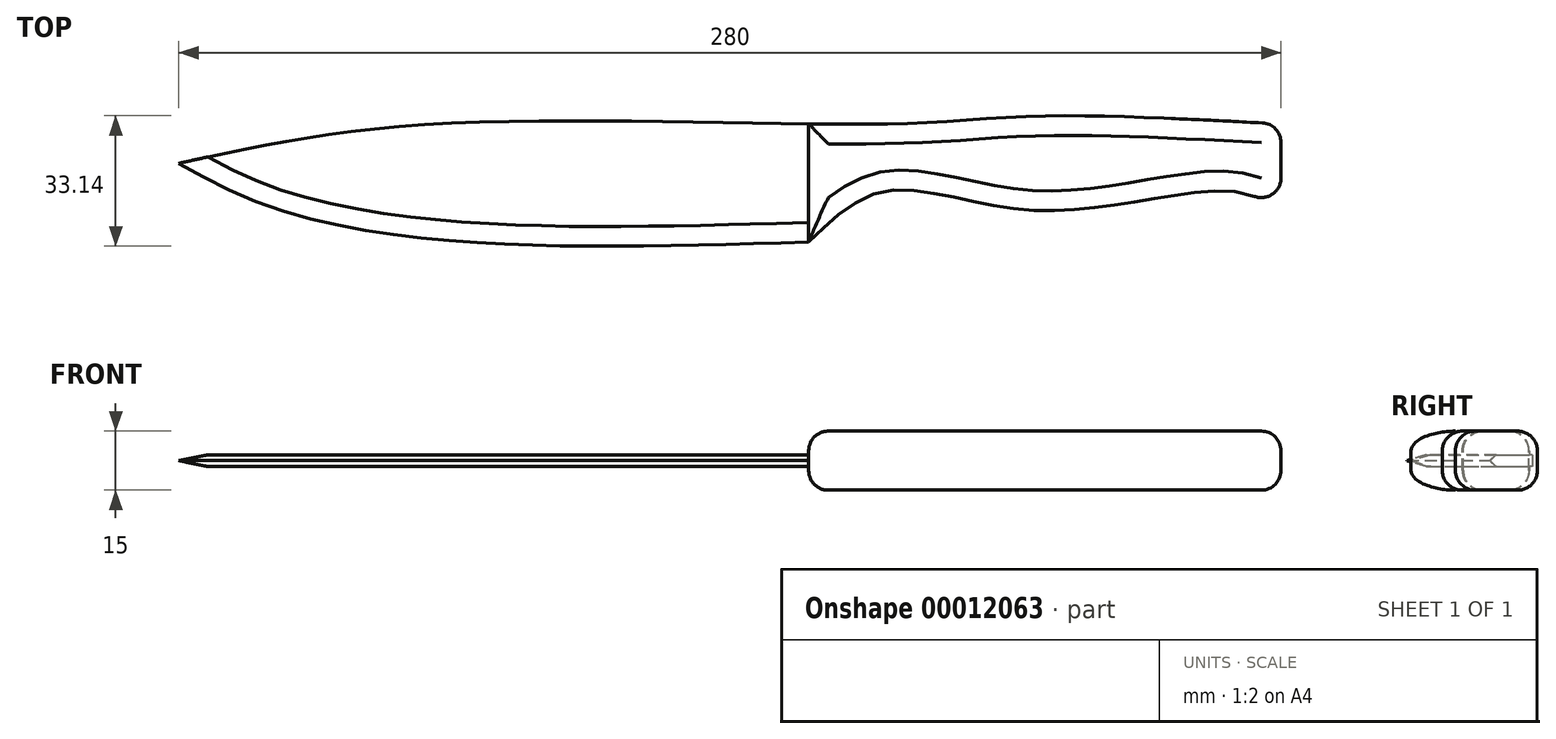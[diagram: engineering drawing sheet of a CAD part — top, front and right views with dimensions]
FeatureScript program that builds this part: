
annotation { "Feature Type Name" : "Feature", "Feature Type Description" : "" }
export const myFeature = defineFeature(function(context is Context, id is Id, definition is map)
    precondition{}
    {
        {
            var Q0;
            Q0=qCreatedBy(makeId("Top.planeOp"),FACE);
            var sketch = newSketch(context, id + "F0", { "sketchPlane" : qUnion([Q0])});
            skLineSegment(sketch, "E0", {"start": v(-162.75, 0) * mm, "end": v(117.25, 0) * mm, "construction": true});
            skLineSegment(sketch, "E1", {"start": v(-2.75, -20) * mm, "end": v(-2.75, 10) * mm});
            skLineSegment(sketch, "E2", {"start": v(17.25, -7) * mm, "end": v(17.25, 10) * mm, "construction": true});
            skLineSegment(sketch, "E3", {"start": v(117.25, 10) * mm, "end": v(117.25, -12) * mm});
            skLineSegment(sketch, "E4", {"start": v(103.55, 0) * mm, "end": v(103.55, -7) * mm, "construction": true});
            skLineSegment(sketch, "E5", {"start": v(55.6, 0) * mm, "end": v(55.6, 12) * mm, "construction": true});
            skLineSegment(sketch, "E6", {"start": v(55.6, 0) * mm, "end": v(55.6, -12) * mm, "construction": true});
            skFitSpline(sketch, "E7", {"points": [v(-162.75, 0) * mm, v(-96.94, 10) * mm, v(17.25, 10) * mm, v(55.6, 12) * mm, v(117.25, 10) * mm], "startDerivative": vector(232.14, 51.12) * mm, "endDerivative": vector(284.39, -15.23) * mm});
            skFitSpline(sketch, "E8", {"points": [v(117.25, -12) * mm, v(103.55, -7) * mm, v(55.6, -12) * mm, v(17.25, -7) * mm, v(-2.75, -20) * mm], "startDerivative": vector(-64.1, 40.3) * mm, "endDerivative": vector(-81.22, -79.08) * mm});
            skFitSpline(sketch, "E9", {"points": [v(-2.75, -20) * mm, v(-89.64, -20) * mm, v(-139.33, -11.16) * mm, v(-162.75, 0) * mm], "startDerivative": vector(-211.22, -6.31) * mm, "endDerivative": vector(-89.85, 50.4) * mm});
            skSolve(sketch);
        }
        {
            var Q0;
            {var subQ0=sQuery(id+"F0.wireOp",EDGE,"E9");Q0=makeQuery(id+"F0.imprint","IMPRINT",FACE,{"disambiguationData":[TD([[makeQuery(id+"F0.imprint","IMPRINT",EDGE,{"derivedFrom":subQ0}),-1.0]])]});}
            extrude(context, id + "F1", {"entities" : qUnion([Q0]), "endBound" : BoundingType.SYMMETRIC, "depth" : 3 * mm});
        }
        {
            var Q0;
            {var subQ4=sQuery(id+"F0.wireOp",EDGE,"E3");Q0=makeQuery(id+"F0.imprint","IMPRINT",FACE,{"disambiguationData":[TD([[makeQuery(id+"F0.imprint","IMPRINT",EDGE,{"derivedFrom":subQ4}),-1.0]])]});}
            extrude(context, id + "F2", {"entities" : qUnion([Q0]), "operationType" : NewBodyOperationType.ADD, "endBound" : BoundingType.SYMMETRIC, "depth" : 15 * mm});
        }
        {
            var Q0;
            Q0=makeQuery(id+"F2.opExtrude","CAP_EDGE",EDGE,{"disambiguationData":[OSD([sQuery(id+"F0.wireOp",EDGE,"E8")])],"isStart":false});
            var Q1;
            Q1=makeQuery(id+"F2.opExtrude","CAP_EDGE",EDGE,{"disambiguationData":[OSD([sQuery(id+"F0.wireOp",EDGE,"E1")])],"isStart":false});
            var Q2;
            Q2=makeQuery(id+"F2.opExtrude","CAP_EDGE",EDGE,{"disambiguationData":[OSD([sQuery(id+"F0.wireOp",EDGE,"E7")])],"isStart":false});
            var Q3;
            Q3=makeQuery(id+"F2.opExtrude","CAP_EDGE",EDGE,{"disambiguationData":[OSD([sQuery(id+"F0.wireOp",EDGE,"E3")])],"isStart":false});
            var Q4;
            Q4=makeQuery(id+"F2.opExtrude","CAP_EDGE",EDGE,{"disambiguationData":[OSD([sQuery(id+"F0.wireOp",EDGE,"E1")])],"isStart":true});
            var Q5;
            Q5=makeQuery(id+"F2.opExtrude","CAP_EDGE",EDGE,{"disambiguationData":[OSD([sQuery(id+"F0.wireOp",EDGE,"E7")])],"isStart":true});
            var Q6;
            Q6=makeQuery(id+"F2.opExtrude","CAP_EDGE",EDGE,{"disambiguationData":[OSD([sQuery(id+"F0.wireOp",EDGE,"E8")])],"isStart":true});
            var Q7;
            Q7=makeQuery(id+"F2.opExtrude","CAP_EDGE",EDGE,{"disambiguationData":[OSD([sQuery(id+"F0.wireOp",EDGE,"E3")])],"isStart":true});
            var Q8;
            Q8=makeQuery(id+"F2.opExtrude","SWEPT_EDGE",EDGE,{"disambiguationData":[OSD([sQuery(id+"F0.wireOp",EDGE,"E3"),sQuery(id+"F0.wireOp",EDGE,"E8")])]});
            var Q9;
            Q9=makeQuery(id+"F2.opExtrude","SWEPT_EDGE",EDGE,{"disambiguationData":[OSD([sQuery(id+"F0.wireOp",EDGE,"E3"),sQuery(id+"F0.wireOp",EDGE,"E7")])]});
            fillet(context, id + "F3", {"entities" : qUnion([Q0, Q1, Q2, Q3, Q4, Q5, Q6, Q7, Q8, Q9]), "radius" : 5 * mm, "tangentPropagation" : true, "allowEdgeOverflow" : false});
        }
        {
            var Q0;
            Q0=makeQuery(id+"F1.opExtrude","CAP_EDGE",EDGE,{"disambiguationData":[OSD([sQuery(id+"F0.wireOp",EDGE,"E9")])],"isStart":true});
            var Q1;
            Q1=makeQuery(id+"F1.opExtrude","CAP_EDGE",EDGE,{"disambiguationData":[OSD([sQuery(id+"F0.wireOp",EDGE,"E9")])],"isStart":false});
            chamfer(context, id + "F4", {"entities" : qUnion([Q0, Q1]), "chamferType" : ChamferType.TWO_OFFSETS, "width1" : 5 * mm, "oppositeDirection" : false, "width2" : 1.5 * mm, "tangentPropagation" : true});
        }
        {
            var Q0;
            Q0=qCreatedBy(makeId("Right.planeOp"),FACE);
            var sketch = newSketch(context, id + "F5", { "sketchPlane" : qUnion([Q0])});
            skLineSegment(sketch, "E10", {"start": v(41.2, 0) * mm, "end": v(53.23, 0) * mm});
            skLineSegment(sketch, "E11", {"start": v(53.23, 0) * mm, "end": v(53.23, 20.85) * mm});
            skLineSegment(sketch, "E12", {"start": v(53.23, 20.85) * mm, "end": v(41.2, 0) * mm});
            skSolve(sketch);
        }
        {
            var Q0;
            Q0=qSketchRegion(id+"F5",true);
            extrude(context, id + "F6", {"entities" : qUnion([Q0]), "depth" : 25 * mm});
        }
        {
            var Q0;
            Q0=makeQuery(id+"F6.opExtrude","SWEPT_BODY",BODY,{"disambiguationData":[OSD([sQuery(id+"F5.wireOp",EDGE,"E10"),sQuery(id+"F5.wireOp",EDGE,"E11"),sQuery(id+"F5.wireOp",EDGE,"E12")])]});
            deleteBodies(context, id + "F7", {"entities" : qUnion([Q0])});
        }
        {
            var Q0;
            Q0=makeQuery(id+"F1.opExtrude","SWEPT_BODY",BODY,{"disambiguationData":[OSD([sQuery(id+"F0.wireOp",EDGE,"E1"),sQuery(id+"F0.wireOp",EDGE,"E7"),sQuery(id+"F0.wireOp",EDGE,"E9")])]});
            transform(context, id + "F8", {"entities" : qUnion([Q0]), "transformType" : TransformType.TRANSLATION_3D, "dx" : 0 * mm, "dy" : 200 * mm, "dz" : 0 * mm, "makeCopy" : false});
        }
    });
